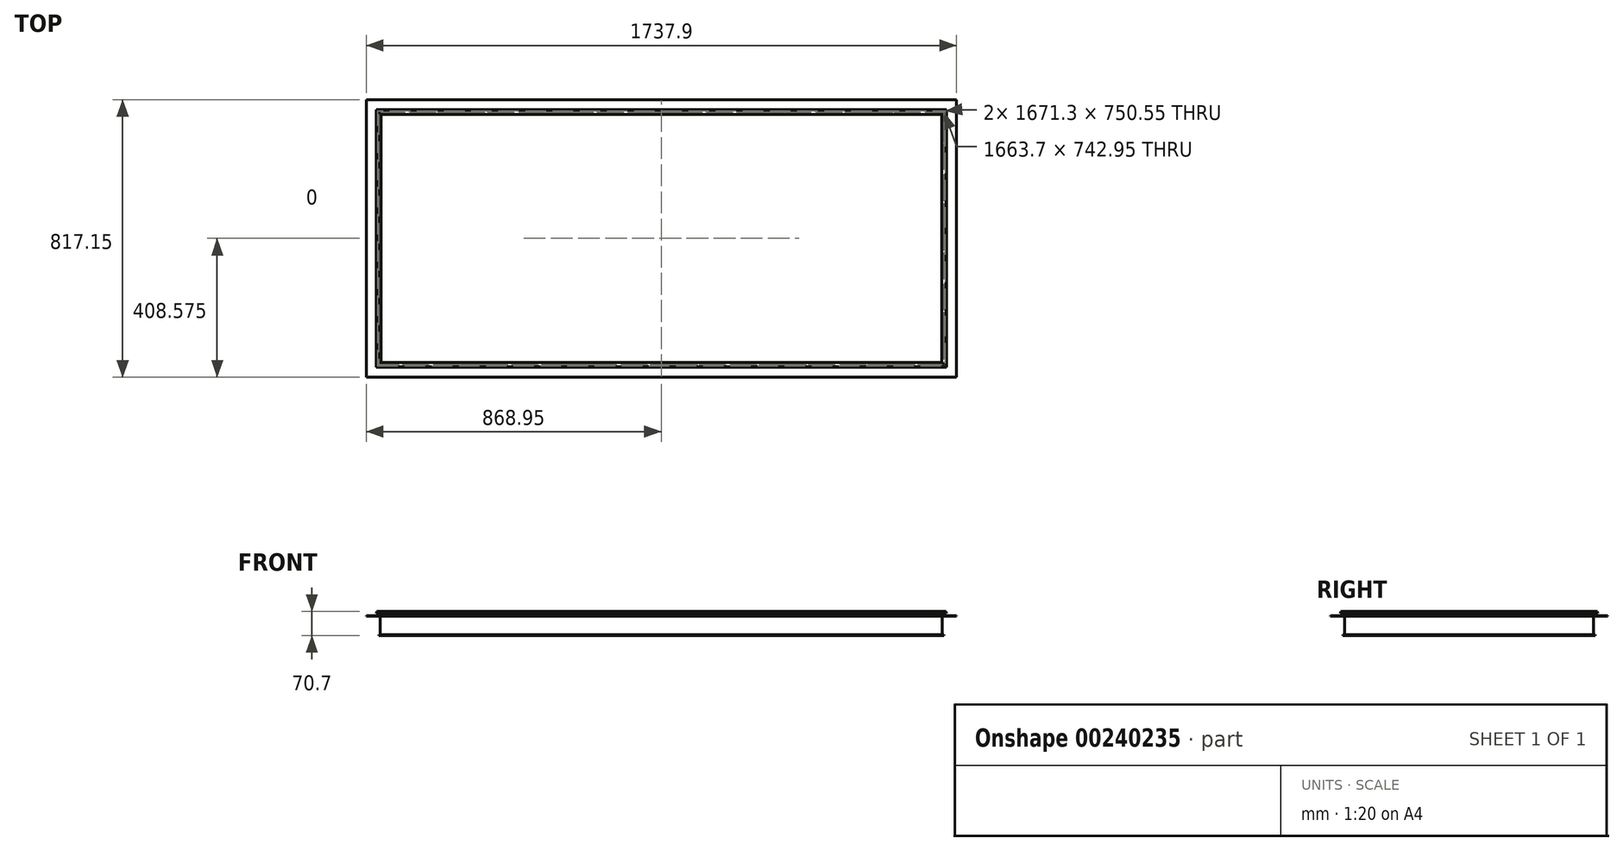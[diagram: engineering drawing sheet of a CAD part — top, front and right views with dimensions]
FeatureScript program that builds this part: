
annotation { "Feature Type Name" : "Feature", "Feature Type Description" : "" }
export const myFeature = defineFeature(function(context is Context, id is Id, definition is map)
    precondition{}
    {
        {
            var Q0;
            Q0=qCreatedBy(makeId("Right.planeOp"),FACE);
            var sketch = newSketch(context, id + "F0", { "sketchPlane" : qUnion([Q0])});
            skLineSegment(sketch, "E0", {"start": v(0, -70.7) * mm, "end": v(0, -6) * mm});
            skLineSegment(sketch, "E1", {"start": v(6, 0) * mm, "end": v(12.2, 0) * mm});
            skLineSegment(sketch, "E2", {"start": v(12.2, 0) * mm, "end": v(12.2, -1.5) * mm});
            skLineSegment(sketch, "E3", {"start": v(12.2, -1.5) * mm, "end": v(9.8, -1.5) * mm});
            skLineSegment(sketch, "E4", {"start": v(9.8, -1.5) * mm, "end": v(9.8, -3.3) * mm});
            skLineSegment(sketch, "E5", {"start": v(9.8, -3.3) * mm, "end": v(13.5, -3.3) * mm});
            skLineSegment(sketch, "E6", {"start": v(13.5, -3.3) * mm, "end": v(13.5, -4.5) * mm});
            skLineSegment(sketch, "E7", {"start": v(13.5, -4.5) * mm, "end": v(9.8, -4.5) * mm});
            skLineSegment(sketch, "E8", {"start": v(9.8, -4.5) * mm, "end": v(9.8, -12.5) * mm});
            skLineSegment(sketch, "E9", {"start": v(9.8, -12.5) * mm, "end": v(43.1, -12.5) * mm});
            skLineSegment(sketch, "E10", {"start": v(43.1, -12.5) * mm, "end": v(43.1, -13.7) * mm});
            skLineSegment(sketch, "E11", {"start": v(43.1, -13.7) * mm, "end": v(8.6, -13.7) * mm});
            skLineSegment(sketch, "E12", {"start": v(8.6, -13.7) * mm, "end": v(8.6, -11.3) * mm});
            skLineSegment(sketch, "E13", {"start": v(8.6, -9.45) * mm, "end": v(8.6, -1.5) * mm});
            skLineSegment(sketch, "E14", {"start": v(8.6, -1.5) * mm, "end": v(6, -1.5) * mm});
            skLineSegment(sketch, "E15", {"start": v(1.5, -6) * mm, "end": v(1.5, -69.5) * mm});
            skLineSegment(sketch, "E16", {"start": v(1.5, -69.5) * mm, "end": v(4.8, -69.5) * mm});
            skLineSegment(sketch, "E17", {"start": v(4.8, -69.5) * mm, "end": v(4.8, -68) * mm});
            skLineSegment(sketch, "E18", {"start": v(4.8, -68) * mm, "end": v(6, -68) * mm});
            skLineSegment(sketch, "E19", {"start": v(6, -68) * mm, "end": v(6, -70.7) * mm});
            skLineSegment(sketch, "E20", {"start": v(6, -70.7) * mm, "end": v(0, -70.7) * mm});
            skLineSegment(sketch, "E21", {"start": v(8.6, -11.3) * mm, "end": v(6.55, -13.7) * mm});
            skLineSegment(sketch, "E22", {"start": v(6.55, -13.7) * mm, "end": v(6, -13.7) * mm});
            skLineSegment(sketch, "E23", {"start": v(6, -13.7) * mm, "end": v(6, -12.5) * mm});
            skLineSegment(sketch, "E24", {"start": v(6, -12.5) * mm, "end": v(8.6, -9.45) * mm});
            skPoint(sketch, "E25.visualSharp", {"position": v(1.5, -1.5) * mm});
            skArc(sketch, "E25.filletArc", {"start": v(6, -1.5) * mm, "mid": v(2.82, -2.82) * mm, "end": v(1.5, -6) * mm});
            skPoint(sketch, "E26.visualSharp", {"position": v(0, 0) * mm});
            skArc(sketch, "E26.filletArc", {"start": v(6, 0) * mm, "mid": v(1.76, -1.76) * mm, "end": v(0, -6) * mm});
            skPoint(sketch, "E27.endSnap0", {"position": v(8.6, -12.5) * mm});
            skPoint(sketch, "E28.endSnap0", {"position": v(5.4, -68) * mm});
            skLineSegment(sketch, "E29", {"start": v(6, 0) * mm, "end": v(5.68, 0) * mm, "construction": true});
            skLineSegment(sketch, "E30", {"start": v(6, -68) * mm, "end": v(6, 11.67) * mm, "construction": true});
            skSolve(sketch);
        }
        {
            var Q0;
            Q0=qCreatedBy(makeId("Top.planeOp"),FACE);
            var sketch = newSketch(context, id + "F1", { "sketchPlane" : qUnion([Q0])});
            skLineSegment(sketch, "E31.bottom", {"start": v(0, 6) * mm, "end": v(1663.7, 6) * mm});
            skLineSegment(sketch, "E31.top", {"start": v(0, -736.95) * mm, "end": v(1663.7, -736.95) * mm});
            skLineSegment(sketch, "E31.right", {"start": v(1663.7, 6) * mm, "end": v(1663.7, -736.95) * mm});
            skLineSegment(sketch, "E32", {"start": v(0, -736.95) * mm, "end": v(0, 6) * mm});
            skSolve(sketch);
        }
        {
            var Q0;
            Q0=makeQuery(id+"F0.imprint","IMPRINT",FACE,{"disambiguationData":[TD([[makeQuery(id+"F0.imprint","IMPRINT",EDGE,{"derivedFrom":sQuery(id+"F0.wireOp",EDGE,"E0")}),-1.0]])]});
            var Q1;
            Q1=sQuery(id+"F1.wireOp",EDGE,"E31.bottom");
            var Q2;
            Q2=sQuery(id+"F1.wireOp",EDGE,"E31.right");
            var Q3;
            Q3=sQuery(id+"F1.wireOp",EDGE,"E31.top");
            var Q4;
            Q4=sQuery(id+"F1.wireOp",EDGE,"E32");
            sweep(context, id + "F2", {"profiles" : qUnion([Q0]), "path" : qUnion([Q1, Q2, Q3, Q4])});
        }
    });
